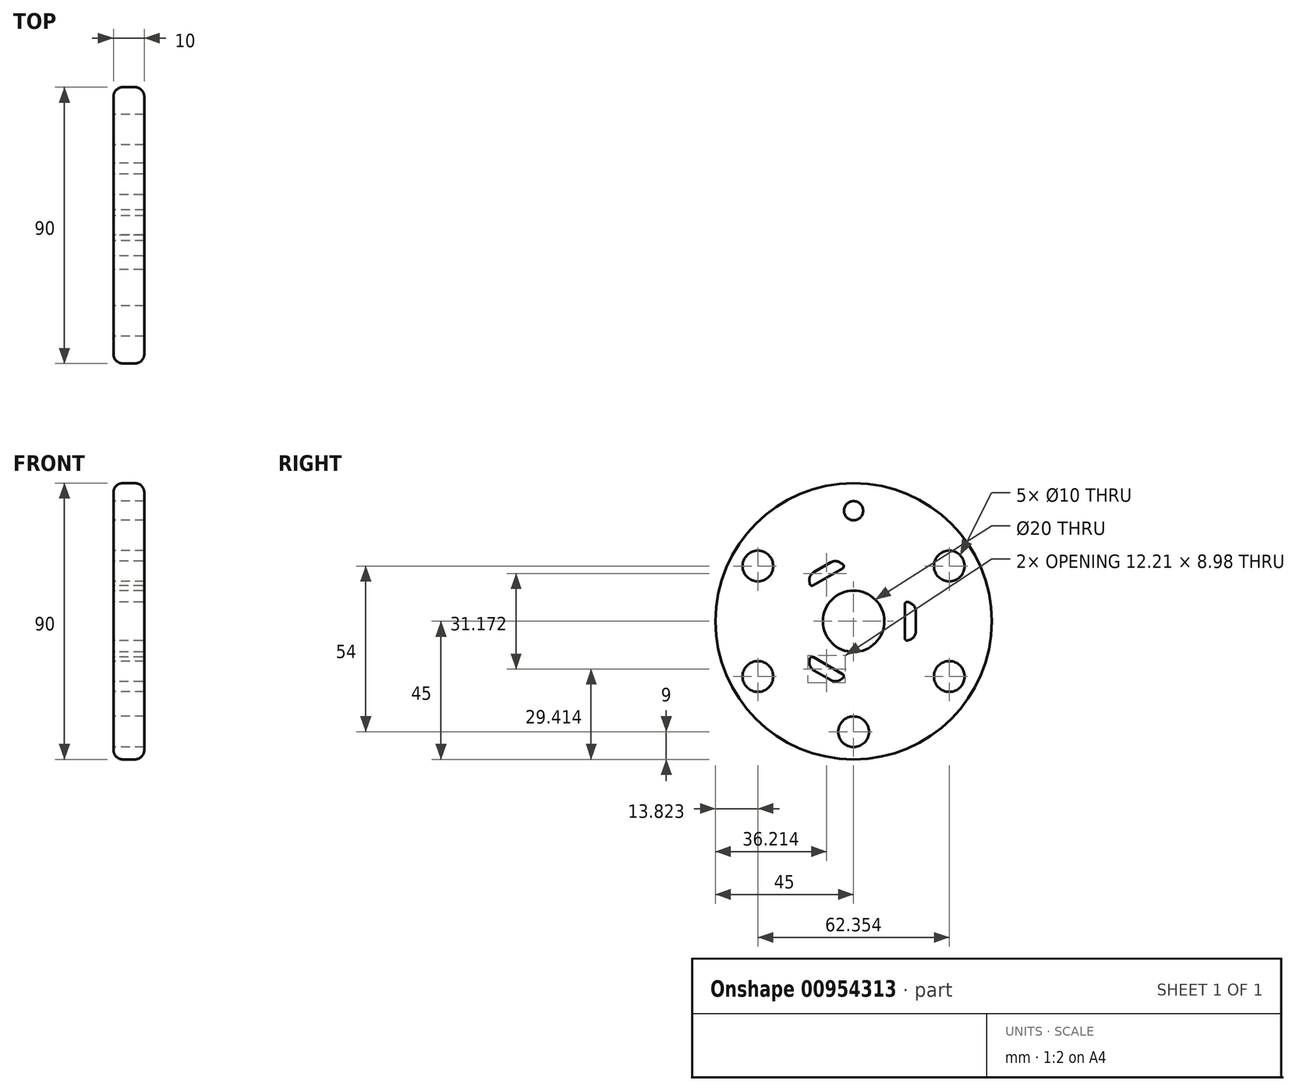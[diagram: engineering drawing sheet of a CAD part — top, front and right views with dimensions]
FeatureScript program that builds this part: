
annotation { "Feature Type Name" : "Feature", "Feature Type Description" : "" }
export const myFeature = defineFeature(function(context is Context, id is Id, definition is map)
    precondition{}
    {
        {
            var Q0;
            Q0=qCreatedBy(makeId("Top.planeOp"),FACE);
            var sketch = newSketch(context, id + "F0", { "sketchPlane" : qUnion([Q0])});
            skLineSegment(sketch, "E0", {"start": v(0, 0) * mm, "end": v(65.59, 0) * mm, "construction": true});
            skLineSegment(sketch, "E1", {"start": v(0, 10) * mm, "end": v(0, 42) * mm});
            skLineSegment(sketch, "E2", {"start": v(3, 45) * mm, "end": v(7, 45) * mm});
            skLineSegment(sketch, "E3", {"start": v(10, 42) * mm, "end": v(10, 10) * mm});
            skPoint(sketch, "E4.visualSharp", {"position": v(0, 45) * mm});
            skArc(sketch, "E4.filletArc", {"start": v(3, 45) * mm, "mid": v(0.88, 44.12) * mm, "end": v(0, 42) * mm});
            skPoint(sketch, "E5.visualSharp", {"position": v(10, 45) * mm});
            skArc(sketch, "E5.filletArc", {"start": v(10, 42) * mm, "mid": v(9.12, 44.12) * mm, "end": v(7, 45) * mm});
            skPoint(sketch, "E6", {"position": v(0, 10) * mm});
            skLineSegment(sketch, "E7", {"start": v(0, 10) * mm, "end": v(10, 10) * mm});
            skPoint(sketch, "E8.start.orphan", {"position": v(10, 0) * mm});
            skSolve(sketch);
        }
        {
            var Q0;
            Q0 = qSketchRegion(id + "F0", true);
            var Q1;
            Q1=sQuery(id+"F0.wireOp",EDGE,"E0");
            revolve(context, id + "F1", {"surfaceOperationType" : NewSurfaceOperationType.NEW, "entities" : qUnion([Q0]), "axis" : qUnion([Q1]), "revolveType" : RevolveType.FULL});
        }
        {
            var Q0;
            Q0=makeQuery(id+"F1.opRevolve","SWEPT_FACE",FACE,{"disambiguationData":[OSD([sQuery(id+"F0.wireOp",EDGE,"E1")])]});
            var sketch = newSketch(context, id + "F2", { "sketchPlane" : qUnion([Q0])});
            skLineSegment(sketch, "E9", {"start": v(0, 0) * mm, "end": v(0, 36) * mm, "construction": true});
            skCircle(sketch, "E10", {"center": v(0, 36) * mm, "radius": 5 * mm});
            skCircle(sketch, "E11", {"center": v(0, 36) * mm, "radius": 3.12 * mm});
            skCircle(sketch, "E12.1.0", {"center": v(-31.18, 18) * mm, "radius": 5 * mm});
            skCircle(sketch, "E12.2.0", {"center": v(-31.18, -18) * mm, "radius": 5 * mm});
            skCircle(sketch, "E12.3.0", {"center": v(0, -36) * mm, "radius": 5 * mm});
            skCircle(sketch, "E12.4.0", {"center": v(31.18, -18) * mm, "radius": 5 * mm});
            skCircle(sketch, "E12.5.0", {"center": v(31.18, 18) * mm, "radius": 5 * mm});
            skPoint(sketch, "E12.center", {"position": v(0, 0) * mm});
            skLineSegment(sketch, "E13", {"start": v(0, 0) * mm, "end": v(31.18, 18) * mm, "construction": true});
            skSolve(sketch);
        }
        {
            var Q0;
            Q0=makeQuery(id+"F2.imprint","IMPRINT",FACE,{"disambiguationData":[TD([[makeQuery(id+"F2.imprint","IMPRINT",EDGE,{"derivedFrom":sQuery(id+"F2.wireOp",EDGE,"E12.1.0")}),1.0]])]});
            var Q1;
            Q1=makeQuery(id+"F2.imprint","IMPRINT",FACE,{"disambiguationData":[TD([[makeQuery(id+"F2.imprint","IMPRINT",EDGE,{"derivedFrom":sQuery(id+"F2.wireOp",EDGE,"E12.2.0")}),1.0]])]});
            var Q2;
            Q2=makeQuery(id+"F2.imprint","IMPRINT",FACE,{"disambiguationData":[TD([[makeQuery(id+"F2.imprint","IMPRINT",EDGE,{"derivedFrom":sQuery(id+"F2.wireOp",EDGE,"E12.3.0")}),1.0]])]});
            var Q3;
            Q3=makeQuery(id+"F2.imprint","IMPRINT",FACE,{"disambiguationData":[TD([[makeQuery(id+"F2.imprint","IMPRINT",EDGE,{"derivedFrom":sQuery(id+"F2.wireOp",EDGE,"E12.4.0")}),1.0]])]});
            var Q4;
            Q4=makeQuery(id+"F2.imprint","IMPRINT",FACE,{"disambiguationData":[TD([[makeQuery(id+"F2.imprint","IMPRINT",EDGE,{"derivedFrom":sQuery(id+"F2.wireOp",EDGE,"E12.5.0")}),1.0]])]});
            extrude(context, id + "F3", {"entities" : qUnion([Q0, Q1, Q2, Q3, Q4]), "operationType" : NewBodyOperationType.REMOVE, "endBound" : BoundingType.UP_TO_NEXT, "oppositeDirection" : true, "depth" : 25 * mm, "offsetDistance" : 25 * mm});
        }
        {
            var Q0;
            Q0=makeQuery(id+"F2.imprint","IMPRINT",FACE,{"disambiguationData":[TD([[makeQuery(id+"F2.imprint","IMPRINT",EDGE,{"derivedFrom":sQuery(id+"F2.wireOp",EDGE,"E11")}),1.0]])]});
            extrude(context, id + "F4", {"entities" : qUnion([Q0]), "operationType" : NewBodyOperationType.REMOVE, "endBound" : BoundingType.UP_TO_NEXT, "oppositeDirection" : true, "depth" : 25 * mm, "offsetDistance" : 25 * mm});
        }
        {
            var Q0;
            Q0=makeQuery(id+"F2.imprint","IMPRINT",FACE,{"disambiguationData":[TD([[makeQuery(id+"F2.imprint","IMPRINT",EDGE,{"derivedFrom":sQuery(id+"F2.wireOp",EDGE,"E10")}),-1.0]])]});
            var sketch = newSketch(context, id + "F5", { "sketchPlane" : qUnion([Q0])});
            skPoint(sketch, "E14", {"position": v(0, 0) * mm});
            skLineSegment(sketch, "E15", {"start": v(0, 0) * mm, "end": v(14.19, 11.08) * mm, "construction": true});
            skLineSegment(sketch, "E16", {"start": v(0, 0) * mm, "end": v(2.5, 17.83) * mm, "construction": true});
            skLineSegment(sketch, "E17", {"start": v(3.58, 17.2) * mm, "end": v(13.1, 11.7) * mm});
            skLineSegment(sketch, "E18", {"start": v(3.52, 18.55) * mm, "end": v(4.2, 19.03) * mm});
            skLineSegment(sketch, "E19", {"start": v(7.43, 19.18) * mm, "end": v(12.9, 16.02) * mm});
            skLineSegment(sketch, "E20", {"start": v(14.38, 13.14) * mm, "end": v(14.3, 12.32) * mm});
            skPoint(sketch, "E21.visualSharp", {"position": v(5.76, 20.14) * mm});
            skArc(sketch, "E21.filletArc", {"start": v(7.43, 19.18) * mm, "mid": v(5.79, 19.58) * mm, "end": v(4.2, 19.03) * mm});
            skPoint(sketch, "E22.visualSharp", {"position": v(14.56, 15.06) * mm});
            skArc(sketch, "E22.filletArc", {"start": v(14.38, 13.14) * mm, "mid": v(14.06, 14.8) * mm, "end": v(12.9, 16.02) * mm});
            skPoint(sketch, "E23.visualSharp", {"position": v(14.19, 11.08) * mm});
            skArc(sketch, "E23.filletArc", {"start": v(13.1, 11.7) * mm, "mid": v(13.88, 11.68) * mm, "end": v(14.3, 12.32) * mm});
            skPoint(sketch, "E24.visualSharp", {"position": v(2.5, 17.83) * mm});
            skArc(sketch, "E24.filletArc", {"start": v(3.52, 18.55) * mm, "mid": v(3.18, 17.86) * mm, "end": v(3.58, 17.2) * mm});
            skArc(sketch, "E25.1.0", {"start": v(-20.32, -3.16) * mm, "mid": v(-19.85, -4.78) * mm, "end": v(-18.57, -5.88) * mm});
            skLineSegment(sketch, "E25.1.1", {"start": v(-17.82, -6.23) * mm, "end": v(-18.57, -5.88) * mm});
            skArc(sketch, "E25.1.2", {"start": v(-17.82, -6.23) * mm, "mid": v(-17.06, -6.17) * mm, "end": v(-16.69, -5.5) * mm});
            skLineSegment(sketch, "E25.1.3", {"start": v(-16.69, -5.5) * mm, "end": v(-16.69, 5.5) * mm});
            skArc(sketch, "E25.1.4", {"start": v(-16.69, 5.5) * mm, "mid": v(-17.06, 6.17) * mm, "end": v(-17.82, 6.23) * mm});
            skLineSegment(sketch, "E25.1.5", {"start": v(-18.57, 5.88) * mm, "end": v(-17.82, 6.23) * mm});
            skArc(sketch, "E25.1.6", {"start": v(-18.57, 5.88) * mm, "mid": v(-19.85, 4.78) * mm, "end": v(-20.32, 3.16) * mm});
            skLineSegment(sketch, "E25.1.7", {"start": v(-20.32, -3.16) * mm, "end": v(-20.32, 3.16) * mm});
            skArc(sketch, "E25.2.0", {"start": v(12.9, -16.02) * mm, "mid": v(14.06, -14.8) * mm, "end": v(14.38, -13.14) * mm});
            skLineSegment(sketch, "E25.2.1", {"start": v(14.3, -12.32) * mm, "end": v(14.38, -13.14) * mm});
            skArc(sketch, "E25.2.2", {"start": v(14.3, -12.32) * mm, "mid": v(13.88, -11.68) * mm, "end": v(13.1, -11.7) * mm});
            skLineSegment(sketch, "E25.2.3", {"start": v(13.1, -11.7) * mm, "end": v(3.58, -17.2) * mm});
            skArc(sketch, "E25.2.4", {"start": v(3.58, -17.2) * mm, "mid": v(3.18, -17.86) * mm, "end": v(3.52, -18.55) * mm});
            skLineSegment(sketch, "E25.2.5", {"start": v(4.2, -19.03) * mm, "end": v(3.52, -18.55) * mm});
            skArc(sketch, "E25.2.6", {"start": v(4.2, -19.03) * mm, "mid": v(5.79, -19.58) * mm, "end": v(7.43, -19.18) * mm});
            skLineSegment(sketch, "E25.2.7", {"start": v(12.9, -16.02) * mm, "end": v(7.43, -19.18) * mm});
            skSolve(sketch);
        }
        {
            var Q0;
            Q0=makeQuery(id+"F5.imprint","IMPRINT",FACE,{"disambiguationData":[TD([[makeQuery(id+"F5.imprint","IMPRINT",EDGE,{"derivedFrom":sQuery(id+"F5.wireOp",EDGE,"E25.1.0")}),1.0]])]});
            var Q1;
            Q1=makeQuery(id+"F5.imprint","IMPRINT",FACE,{"disambiguationData":[TD([[makeQuery(id+"F5.imprint","IMPRINT",EDGE,{"derivedFrom":sQuery(id+"F5.wireOp",EDGE,"E17")}),1.0]])]});
            var Q2;
            Q2=makeQuery(id+"F5.imprint","IMPRINT",FACE,{"disambiguationData":[TD([[makeQuery(id+"F5.imprint","IMPRINT",EDGE,{"derivedFrom":sQuery(id+"F5.wireOp",EDGE,"E25.2.0")}),1.0]])]});
            extrude(context, id + "F6", {"entities" : qUnion([Q0, Q1, Q2]), "operationType" : NewBodyOperationType.REMOVE, "endBound" : BoundingType.UP_TO_NEXT, "oppositeDirection" : true, "depth" : 25 * mm, "offsetDistance" : 25 * mm});
        }
        {
            var Q0;
            Q0=makeQuery(id+"F1.opRevolve","SWEPT_EDGE",EDGE,{"disambiguationData":[OSD([sQuery(id+"F0.wireOp",EDGE,"E1"),sQuery(id+"F0.wireOp",EDGE,"E7")])]});
            var Q1;
            Q1=makeQuery(id+"F1.opRevolve","SWEPT_FACE",FACE,{"disambiguationData":[OSD([sQuery(id+"F0.wireOp",EDGE,"E7")])]});
            var Q2;
            Q2=makeQuery(id+"F6.boolean.opBoolean","COPY",FACE,{"derivedFrom":makeQuery(id+"F6.opExtrude","SWEPT_FACE",FACE,{"disambiguationData":[OSD([sQuery(id+"F5.wireOp",EDGE,"E25.1.7")])]})});
            var Q3;
            Q3=makeQuery(id+"F6.boolean.opBoolean","COPY",FACE,{"derivedFrom":makeQuery(id+"F6.opExtrude","SWEPT_FACE",FACE,{"disambiguationData":[OSD([sQuery(id+"F5.wireOp",EDGE,"E19")])]})});
            var Q4;
            Q4=makeQuery(id+"F6.boolean.opBoolean","COPY",FACE,{"derivedFrom":makeQuery(id+"F6.opExtrude","SWEPT_FACE",FACE,{"disambiguationData":[OSD([sQuery(id+"F5.wireOp",EDGE,"E25.2.3")])]})});
            fillet(context, id + "F7", {"entities" : qUnion([Q0, Q1, Q2, Q3, Q4]), "radius" : 0.5 * mm, "tangentPropagation" : true, "allowEdgeOverflow" : false});
        }
    });
